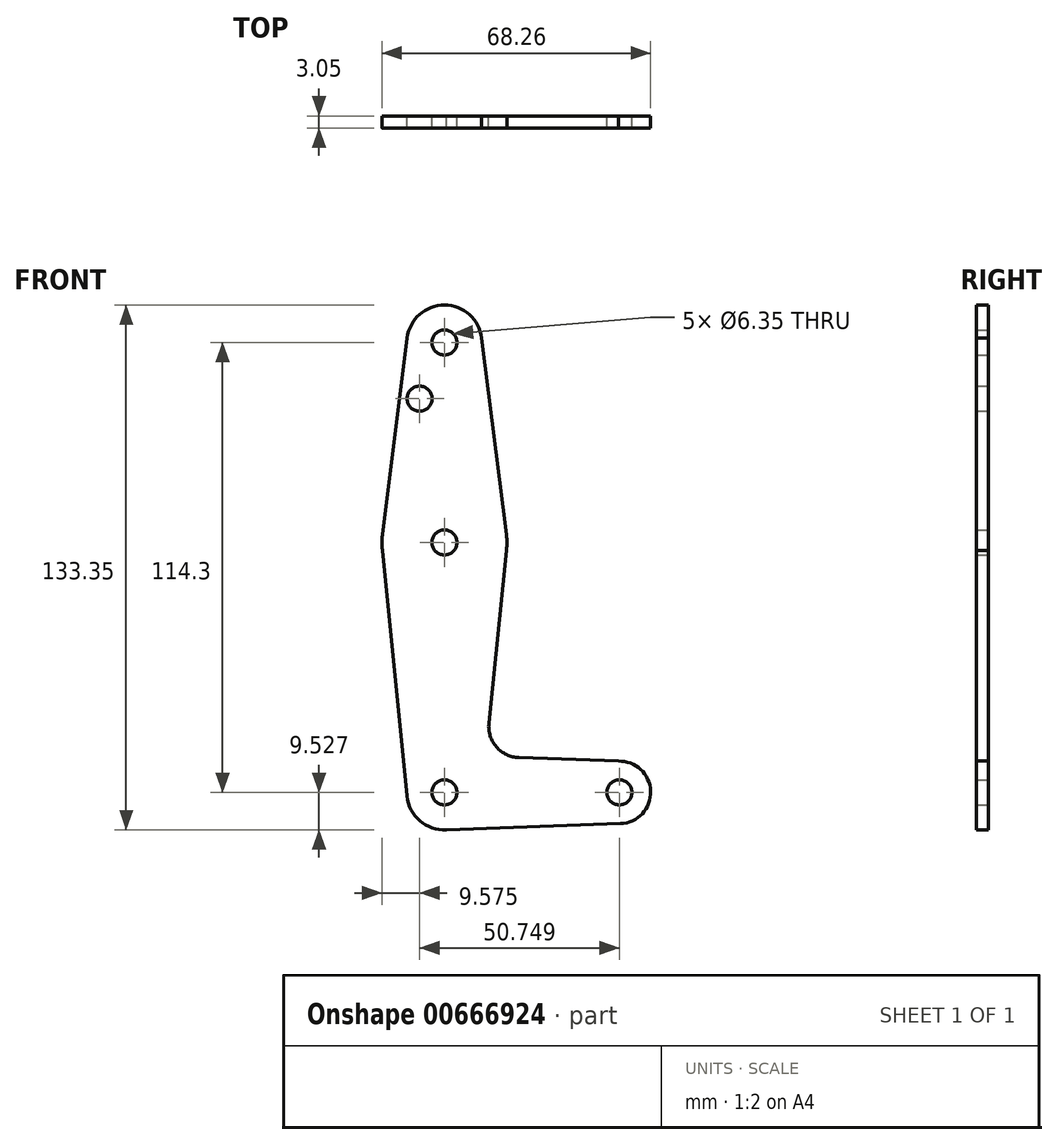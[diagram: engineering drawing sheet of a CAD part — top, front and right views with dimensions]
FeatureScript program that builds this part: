
annotation { "Feature Type Name" : "Feature", "Feature Type Description" : "" }
export const myFeature = defineFeature(function(context is Context, id is Id, definition is map)
    precondition{}
    {
        {
            var Q0;
            Q0=qCreatedBy(makeId("Front.planeOp"),FACE);
            var sketch = newSketch(context, id + "F0", { "sketchPlane" : qUnion([Q0])});
            skLineSegment(sketch, "E0", {"start": v(-34.56, 75.17) * mm, "end": v(-34.56, 18.02) * mm});
            skCircle(sketch, "E1", {"center": v(-34.56, 75.17) * mm, "radius": 9.53 * mm});
            skCircle(sketch, "E2", {"center": v(-34.56, -39.13) * mm, "radius": 9.53 * mm});
            skCircle(sketch, "E3", {"center": v(9.9, -39.13) * mm, "radius": 7.94 * mm});
            skPoint(sketch, "E4.center.orphan", {"position": v(-34.56, 18.02) * mm});
            skLineSegment(sketch, "E5", {"start": v(-34.56, 18.02) * mm, "end": v(-34.56, -29.6) * mm});
            skCircle(sketch, "E6", {"center": v(-34.56, 24.37) * mm, "radius": 15.88 * mm});
            skLineSegment(sketch, "E7", {"start": v(-44.01, 76.3) * mm, "end": v(-50.3, 26.35) * mm});
            skLineSegment(sketch, "E8", {"start": v(-50.3, 22.38) * mm, "end": v(-44.03, -40.08) * mm});
            skLineSegment(sketch, "E9", {"start": v(-34.37, -48.66) * mm, "end": v(10.18, -47.06) * mm});
            skLineSegment(sketch, "E10", {"start": v(10.18, -31.2) * mm, "end": v(9.61, -31.2) * mm});
            skLineSegment(sketch, "E11", {"start": v(-25.12, 76.46) * mm, "end": v(-18.8, 26.35) * mm});
            skLineSegment(sketch, "E12", {"start": v(-18.8, 22.38) * mm, "end": v(-23.25, -21.54) * mm});
            skLineSegment(sketch, "E13", {"start": v(9.61, -31.2) * mm, "end": v(-15.63, -30.3) * mm});
            skCircle(sketch, "E14", {"center": v(-34.56, 75.17) * mm, "radius": 3.18 * mm});
            skCircle(sketch, "E15", {"center": v(-40.86, 60.9) * mm, "radius": 3.18 * mm});
            skCircle(sketch, "E16", {"center": v(-34.56, 24.37) * mm, "radius": 3.18 * mm});
            skCircle(sketch, "E17", {"center": v(-34.56, -39.13) * mm, "radius": 3.18 * mm});
            skCircle(sketch, "E18", {"center": v(9.9, -39.13) * mm, "radius": 3.18 * mm});
            skArc(sketch, "E19.filletArc", {"start": v(-23.25, -21.54) * mm, "mid": v(-21.33, -27.57) * mm, "end": v(-15.63, -30.3) * mm});
            skLineSegment(sketch, "E20.trimOffspring", {"start": v(-25.03, -39.13) * mm, "end": v(9.9, -39.13) * mm});
            skSolve(sketch);
        }
        {
            var Q0;
            Q0 = qSketchRegion(id + "F0", true);
            extrude(context, id + "F1", {"entities" : qUnion([Q0]), "depth" : 3.05 * mm, "offsetDistance" : 25.4 * mm});
        }
    });
